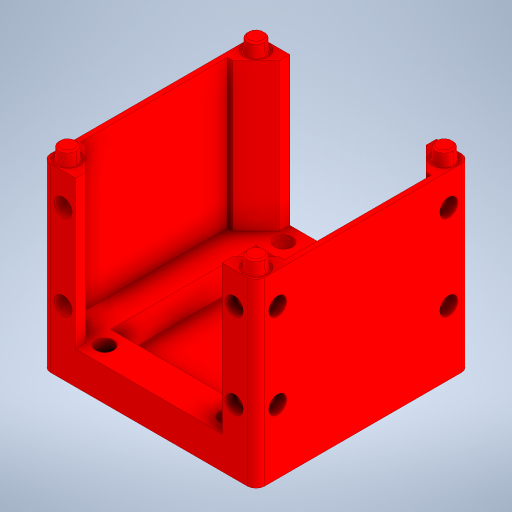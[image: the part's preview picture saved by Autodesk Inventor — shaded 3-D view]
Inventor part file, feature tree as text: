
AUTODESK INVENTOR PART (.ipt)
format: ipt  version: 2023.1 (Build 271208000, 208)  size: 419,840 bytes
history: native  units: mm
features: extrude x8, chamfer x7, sketch x4, projected_geometry x2, pattern_linear x1, pattern_circular x1, fillet x1
ambient origin geometry x8: Origin, YZ Plane, XZ Plane, XY Plane, X Axis, Y Axis, Z Axis, Center Point
bodies: Solid1 (feature_tree)
feature tree (24):
  sketch  "Sketch1"  dims[d0=49.8mm d1=49.8mm]
  extrude  "Extrusion1"  Depth=49.8mm
  extrude  "Extrusion2"  Depth=8.0mm
  extrude  "Extrusion3"  Depth=4.1mm
  extrude  "Extrusion4"  Depth=1.175mm
  chamfer  "Chamfer1"  Distance=3.0mm
  chamfer  "Chamfer2"  Distance=4.2625mm
  chamfer  "Chamfer3"  Distance=0.675mm
  chamfer  "Chamfer4"  Distance=7.85mm
  chamfer  "Chamfer5"  Distance=7.85mm
  chamfer  "Chamfer6"  Distance=5.5mm
  sketch  "Sketch2"  dims[d2=8.0mm d3=10.5mm]
  extrude  "Extrusion5"  Depth=5.5mm
  extrude  "Extrusion6"  Depth=1.175mm TaperAngle=360.0deg
  pattern_linear  "Rectangular Pattern1"  Spacing1=7.7mm  [1 undecoded]
  pattern_circular  "Circular Pattern1"  [2 undecoded]
  extrude  "Extrusion7"  Depth=0.375mm TaperAngle=0.0deg
  fillet  "Fillet1"  Radius=3.25mm
  chamfer  "Chamfer7"  Distance=2.0mm Angle=45.0deg
  extrude  "Extrusion8"  Depth=0.375mm TaperAngle=45.0deg
  sketch  "Sketch3"  dims[d4=10.5mm d5=4.1mm]
  projected_geometry  "Projected Loop1"
  sketch  "Sketch4"  dims[d6=4.15mm d7=3.0mm d8=3.0mm d9=4.2625mm d10=0.675mm d11=7.85mm d12=7.85mm d13=5.5mm d14=5.5mm d15=40.0mm d17=360.0deg d19=7.7mm d20=0.0mm d21=34.4mm d22=0.0mm d23=0.375mm d24=0.0mm d25=3.25mm d26=0.0mm d27=0.5mm d28=2.0mm d29=45.0deg d30=0.375mm d31=2.0mm d32=45.0deg d33=2.75mm d34=2.0mm d35=0.436332mm d36=2.75mm d37=2.0mm d38=0.436332mm d39=2.75mm d40=2.0mm d41=0.436332mm d42=2.75mm d43=2.0mm d44=0.436332mm d45=10.0mm d46=3.125mm d47=5.0mm d48=15.0mm d49=4.125mm d50=3.25mm d51=0.0mm d52=2.5mm d53=0.0mm d54=20.0mm d56=19.8mm d57=40.0mm d58=360.0deg d60=3.75mm d61=5.0mm d62=5.0mm d63=5.4125mm d64=0.0mm d65=2.0mm d66=0.025mm d67=2.0mm d68=0.436332mm d69=1.175mm d70=0.0mm]
  projected_geometry  "Projected Loop2"
note: 3 required parameter values undecoded (feature->parameter linkage not recoverable at this tier; creation-order binding heuristic only, values carry confidence <= 0.55)
